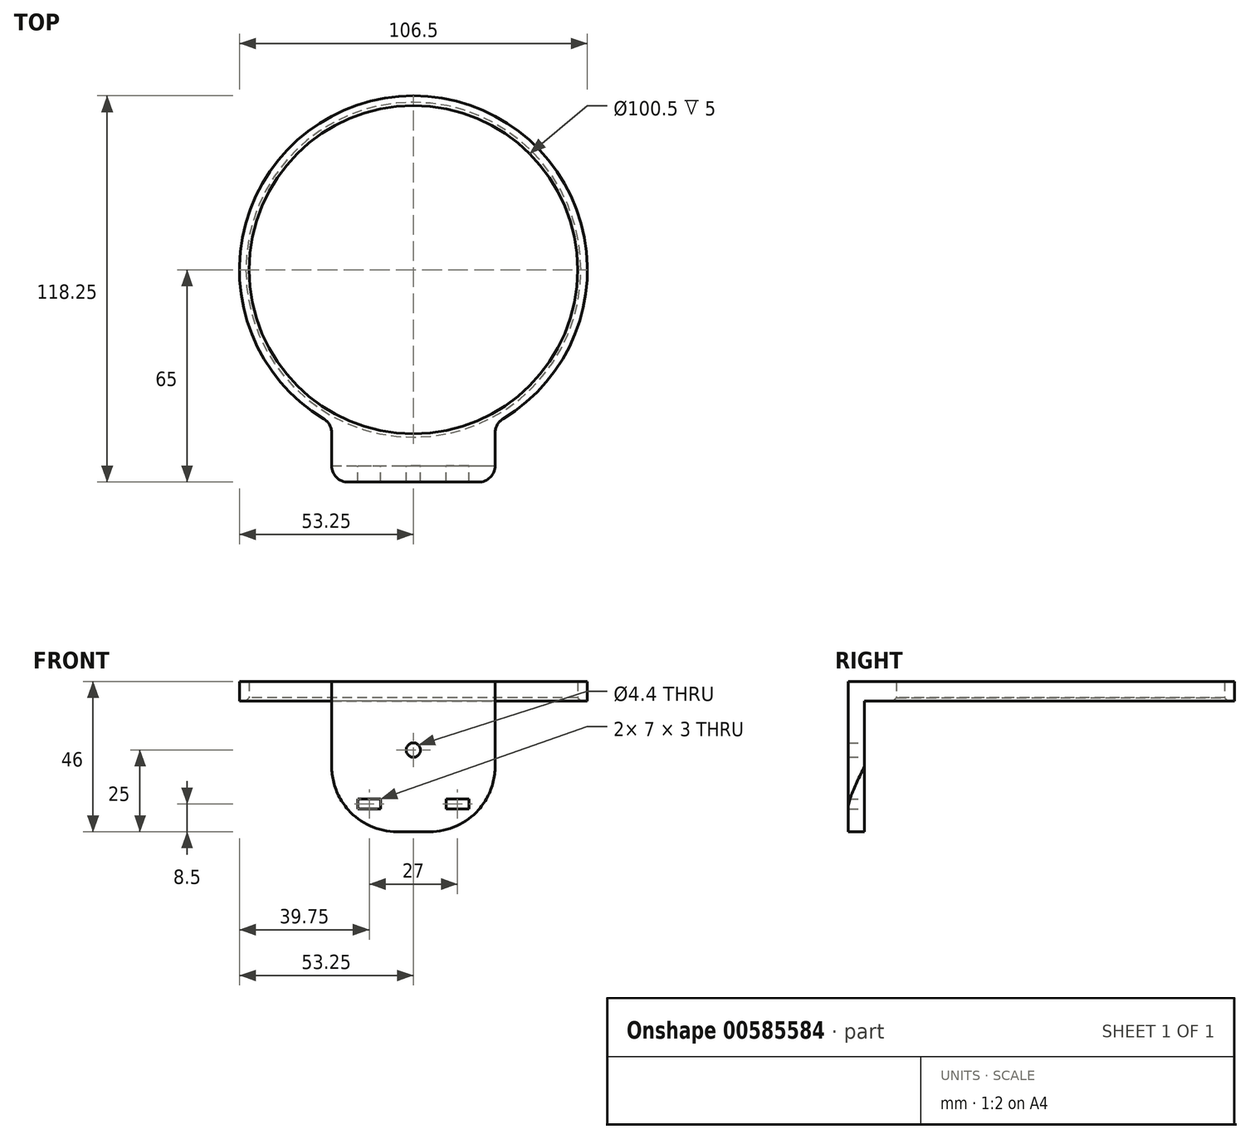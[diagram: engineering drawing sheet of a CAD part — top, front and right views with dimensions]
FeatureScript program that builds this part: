
annotation { "Feature Type Name" : "Feature", "Feature Type Description" : "" }
export const myFeature = defineFeature(function(context is Context, id is Id, definition is map)
    precondition{}
    {
        {
            var Q0;
            Q0=qCreatedBy(makeId("Top.planeOp"),FACE);
            var sketch = newSketch(context, id + "F0", { "sketchPlane" : qUnion([Q0])});
            skCircle(sketch, "E0", {"center": v(0, 0) * mm, "radius": 50.25 * mm});
            skCircle(sketch, "E1.0", {"center": v(0, 0) * mm, "radius": 53.25 * mm});
            skLineSegment(sketch, "E2", {"start": v(-25, -47.02) * mm, "end": v(-25, -65) * mm});
            skLineSegment(sketch, "E3", {"start": v(-25, -65) * mm, "end": v(0, -65) * mm});
            skLineSegment(sketch, "E4", {"start": v(0, 0) * mm, "end": v(0, -65) * mm, "construction": true});
            skLineSegment(sketch, "E5.MirrorCS", {"start": v(25, -47.02) * mm, "end": v(25, -65) * mm});
            skLineSegment(sketch, "E6.MirrorCS", {"start": v(25, -65) * mm, "end": v(0, -65) * mm});
            skLineSegment(sketch, "E7", {"start": v(-25, -60) * mm, "end": v(25, -60) * mm});
            skSolve(sketch);
        }
        {
            var Q0;
            Q0=makeQuery(id+"F0.imprint","IMPRINT",FACE,{"disambiguationData":[TD([[makeQuery(id+"F0.imprint","IMPRINT",EDGE,{"derivedFrom":sQuery(id+"F0.wireOp",EDGE,"E0")}),-1.0]])]});
            var Q1;
            {var subQ5=sQuery(id+"F0.wireOp",EDGE,"E7");Q1=makeQuery(id+"F0.imprint","IMPRINT",FACE,{"disambiguationData":[TD([[makeQuery(id+"F0.imprint","IMPRINT",EDGE,{"derivedFrom":subQ5}),1.0]])]});}
            var Q2;
            {var subQ3=sQuery(id+"F0.wireOp",EDGE,"E3");Q2=makeQuery(id+"F0.imprint","IMPRINT",FACE,{"disambiguationData":[TD([[makeQuery(id+"F0.imprint","IMPRINT",EDGE,{"derivedFrom":subQ3}),1.0]])]});}
            extrude(context, id + "F1", {"entities" : qUnion([Q0, Q1, Q2]), "depth" : 6 * mm, "offsetDistance" : 25 * mm});
        }
        {
            var Q0;
            {var subQ3=sQuery(id+"F0.wireOp",EDGE,"E3");Q0=makeQuery(id+"F0.imprint","IMPRINT",FACE,{"disambiguationData":[TD([[makeQuery(id+"F0.imprint","IMPRINT",EDGE,{"derivedFrom":subQ3}),1.0]])]});}
            extrude(context, id + "F2", {"entities" : qUnion([Q0]), "operationType" : NewBodyOperationType.ADD, "oppositeDirection" : true, "depth" : 40 * mm, "offsetDistance" : 25 * mm});
        }
        {
            var Q0;
            Q0=makeQuery(id+"F2.opExtrude","SWEPT_FACE",FACE,{"disambiguationData":[OSD([sQuery(id+"F0.wireOp",EDGE,"E7")])]});
            var sketch = newSketch(context, id + "F3", { "sketchPlane" : qUnion([Q0])});
            skLineSegment(sketch, "E8", {"start": v(0, 0) * mm, "end": v(0, -40) * mm, "construction": true});
            skPoint(sketch, "E9", {"position": v(0, -15) * mm});
            skLineSegment(sketch, "E10", {"start": v(-25, -30) * mm, "end": v(25, -30) * mm, "construction": true});
            skLineSegment(sketch, "E11.bottom", {"start": v(-17, -30) * mm, "end": v(-10, -30) * mm});
            skLineSegment(sketch, "E11.top", {"start": v(-17, -33) * mm, "end": v(-10, -33) * mm});
            skLineSegment(sketch, "E11.left", {"start": v(-17, -30) * mm, "end": v(-17, -33) * mm});
            skLineSegment(sketch, "E11.right", {"start": v(-10, -30) * mm, "end": v(-10, -33) * mm});
            skLineSegment(sketch, "E12.MirrorCS", {"start": v(10, -30) * mm, "end": v(10, -33) * mm});
            skLineSegment(sketch, "E13.MirrorCS", {"start": v(17, -33) * mm, "end": v(10, -33) * mm});
            skLineSegment(sketch, "E14.MirrorCS", {"start": v(17, -30) * mm, "end": v(17, -33) * mm});
            skLineSegment(sketch, "E15.MirrorCS", {"start": v(25, -30) * mm, "end": v(-25, -30) * mm, "construction": true});
            skLineSegment(sketch, "E16.MirrorCS", {"start": v(17, -30) * mm, "end": v(10, -30) * mm});
            skSolve(sketch);
        }
        {
            var Q0;
            Q0=sQuery(id+"F3.wireOp",VERTEX,"E9");
            var Q1;
            Q1=makeQuery(id+"F1.opExtrude","SWEPT_BODY",BODY,{"disambiguationData":[OSD([sQuery(id+"F0.wireOp",EDGE,"E0"),sQuery(id+"F0.wireOp",EDGE,"E1.0"),sQuery(id+"F0.wireOp",EDGE,"E2"),sQuery(id+"F0.wireOp",EDGE,"E3"),sQuery(id+"F0.wireOp",EDGE,"E5.MirrorCS"),sQuery(id+"F0.wireOp",EDGE,"E6.MirrorCS")])]});
            hole(context, id + "F4", {"style" : HoleStyle.SIMPLE, "endStyle" : HoleEndStyle.THROUGH, "standardTappedOrClearance" : lookupTablePath({ "standard" : "ISO", "fit" : "Normal", "size" : "M4", "type" : "Clearance" }), "standardBlindInLast" : lookupTablePath({ "fit" : "Standard", "standard" : "ISO", "size" : "M4", "type" : "Clearance" }), "holeDiameter" : 4.4 * mm, "majorDiameter" : 5 * mm, "isTappedThrough" : true, "tappedDepth" : 12 * mm, "tapClearance" : 3, "locations" : qUnion([Q0]), "scope" : qUnion([Q1])});
        }
        {
            var Q0;
            Q0=makeQuery(id+"F3.imprint","IMPRINT",FACE,{"disambiguationData":[TD([[makeQuery(id+"F3.imprint","IMPRINT",EDGE,{"derivedFrom":sQuery(id+"F3.wireOp",EDGE,"E11.bottom")}),-1.0]])]});
            var Q1;
            Q1=makeQuery(id+"F3.imprint","IMPRINT",FACE,{"disambiguationData":[TD([[makeQuery(id+"F3.imprint","IMPRINT",EDGE,{"derivedFrom":sQuery(id+"F3.wireOp",EDGE,"E12.MirrorCS")}),1.0]])]});
            extrude(context, id + "F5", {"entities" : qUnion([Q0, Q1]), "operationType" : NewBodyOperationType.REMOVE, "oppositeDirection" : true, "depth" : 25 * mm, "offsetDistance" : 25 * mm});
        }
        {
            var Q0;
            Q0=makeQuery(id+"F1.opExtrude","SWEPT_EDGE",EDGE,{"disambiguationData":[OSD([sQuery(id+"F0.wireOp",EDGE,"E1.0"),sQuery(id+"F0.wireOp",EDGE,"E2")])]});
            var Q1;
            Q1=makeQuery(id+"F1.opExtrude","SWEPT_EDGE",EDGE,{"disambiguationData":[OSD([sQuery(id+"F0.wireOp",EDGE,"E1.0"),sQuery(id+"F0.wireOp",EDGE,"E5.MirrorCS")])]});
            var Q2;
            Q2=makeQuery(id+"F2.opExtrude","CAP_EDGE",EDGE,{"disambiguationData":[OSD([sQuery(id+"F0.wireOp",EDGE,"E7")])],"isStart":true});
            fillet(context, id + "F6", {"entities" : qUnion([Q0, Q1, Q2]), "radius" : 5 * mm, "tangentPropagation" : true, "allowEdgeOverflow" : false});
        }
        {
            var Q0;
            Q0=makeQuery(id+"F2.opExtrude","CAP_EDGE",EDGE,{"disambiguationData":[OSD([sQuery(id+"F0.wireOp",EDGE,"E5.MirrorCS")])],"isStart":false});
            var Q1;
            Q1=makeQuery(id+"F2.opExtrude","CAP_EDGE",EDGE,{"disambiguationData":[OSD([sQuery(id+"F0.wireOp",EDGE,"E2")])],"isStart":false});
            fillet(context, id + "F7", {"entities" : qUnion([Q0, Q1]), "radius" : 20 * mm, "tangentPropagation" : true, "allowEdgeOverflow" : false});
        }
        {
            var Q0;
            {var subQ0=sQuery(id+"F0.wireOp",EDGE,"E6.MirrorCS");var subQ1=sQuery(id+"F0.wireOp",EDGE,"E5.MirrorCS");Q0=makeQuery(id+"F2.boolean.opBoolean","MERGE",EDGE,{"derivedFrom":[makeQuery(id+"F1.opExtrude","SWEPT_EDGE",EDGE,{"disambiguationData":[OSD([subQ1,subQ0])]}),makeQuery(id+"F2.opExtrude","SWEPT_EDGE",EDGE,{"disambiguationData":[OSD([subQ1,subQ0])]})]});}
            var Q1;
            {var subQ0=sQuery(id+"F0.wireOp",EDGE,"E3");var subQ1=sQuery(id+"F0.wireOp",EDGE,"E2");Q1=makeQuery(id+"F2.boolean.opBoolean","MERGE",EDGE,{"derivedFrom":[makeQuery(id+"F1.opExtrude","SWEPT_EDGE",EDGE,{"disambiguationData":[OSD([subQ1,subQ0])]}),makeQuery(id+"F2.opExtrude","SWEPT_EDGE",EDGE,{"disambiguationData":[OSD([subQ1,subQ0])]})]});}
            fillet(context, id + "F8", {"entities" : qUnion([Q0, Q1]), "radius" : 5 * mm, "allowEdgeOverflow" : false});
        }
        {
            var Q0;
            Q0=makeQuery(id+"F1.opExtrude","CAP_EDGE",EDGE,{"disambiguationData":[OSD([sQuery(id+"F0.wireOp",EDGE,"E0")])],"isStart":true});
            chamfer(context, id + "F9", {"entities" : qUnion([Q0]), "width" : 1 * mm, "tangentPropagation" : true});
        }
    });
